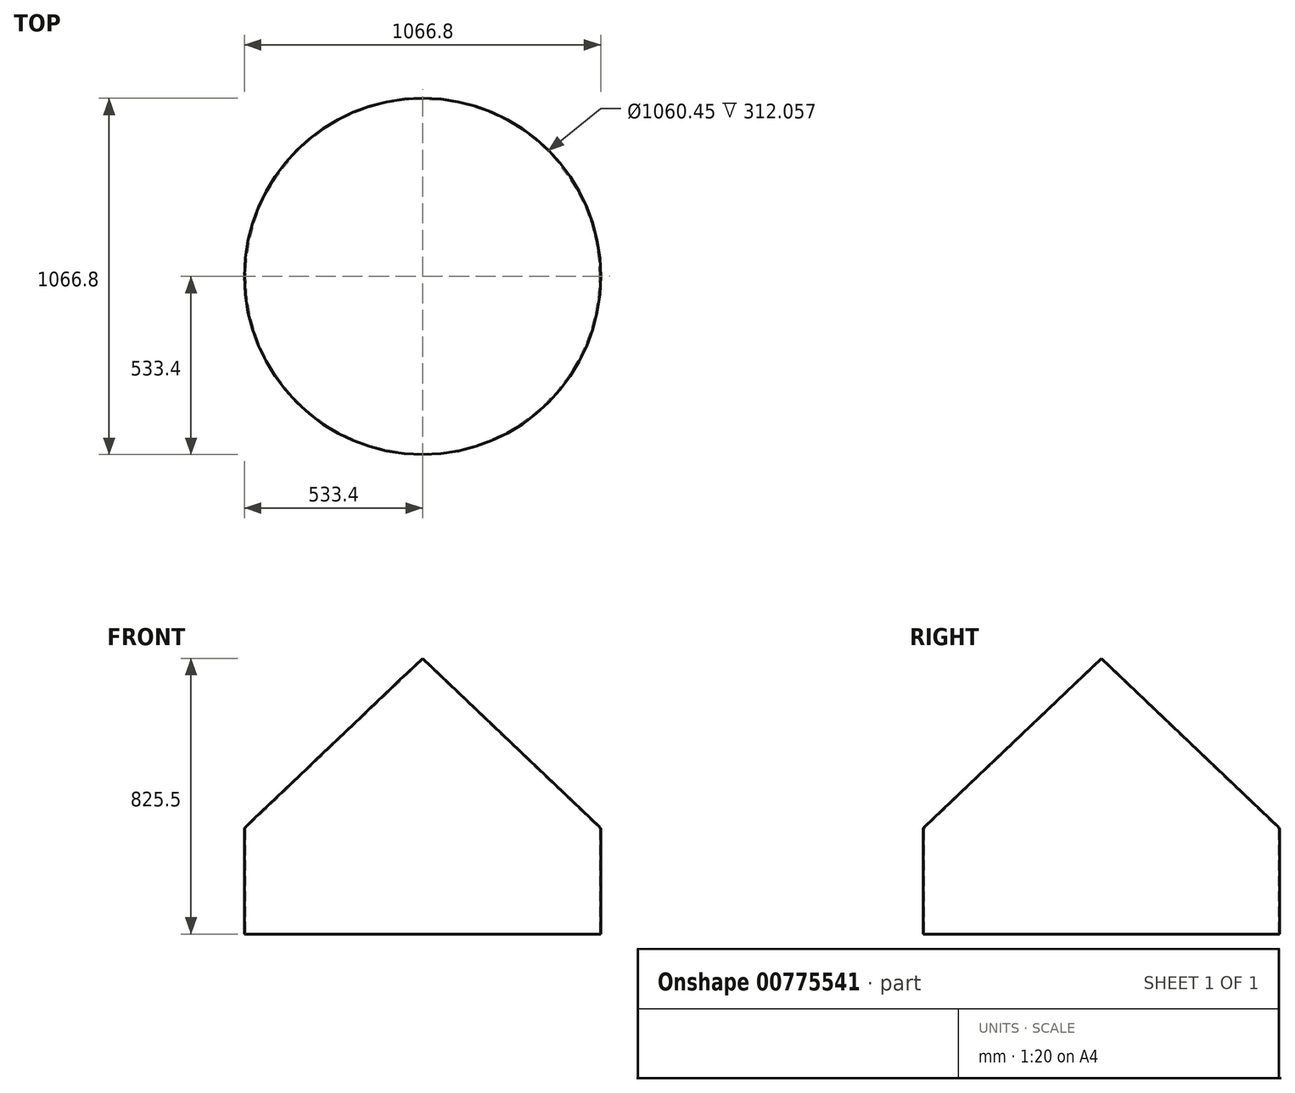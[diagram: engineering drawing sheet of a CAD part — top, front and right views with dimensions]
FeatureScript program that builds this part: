
annotation { "Feature Type Name" : "Feature", "Feature Type Description" : "" }
export const myFeature = defineFeature(function(context is Context, id is Id, definition is map)
    precondition{}
    {
        {
            var Q0;
            Q0=qCreatedBy(makeId("Front.planeOp"),FACE);
            var sketch = newSketch(context, id + "F0", { "sketchPlane" : qUnion([Q0])});
            skLineSegment(sketch, "E0.bottom", {"start": v(0, 0) * mm, "end": v(533.4, 0) * mm});
            skLineSegment(sketch, "E0.left", {"start": v(0, 0) * mm, "end": v(0, 825.5) * mm});
            skLineSegment(sketch, "E0.right", {"start": v(533.4, 0) * mm, "end": v(533.4, 317.5) * mm});
            skLineSegment(sketch, "E1", {"start": v(533.4, 317.5) * mm, "end": v(0, 825.5) * mm});
            skSolve(sketch);
        }
        {
            var Q0;
            Q0 = qSketchRegion(id + "F0", true);
            var Q1;
            Q1=sQuery(id+"F0.wireOp",EDGE,"E0.left");
            revolve(context, id + "F1", {"surfaceOperationType" : NewSurfaceOperationType.NEW, "entities" : qUnion([Q0]), "axis" : qUnion([Q1]), "revolveType" : RevolveType.FULL});
        }
        {
            var Q0;
            Q0=makeQuery(id+"F1.opRevolve","SWEPT_EDGE",EDGE,{"disambiguationData":[OSD([sQuery(id+"F0.wireOp",EDGE,"E0.right"),sQuery(id+"F0.wireOp",EDGE,"E1")])]});
            fillet(context, id + "F2", {"entities" : qUnion([Q0]), "radius" : 12.7 * mm, "tangentPropagation" : true, "allowEdgeOverflow" : false});
        }
        {
            var Q0;
            Q0=makeQuery(id+"F1.opRevolve","SWEPT_FACE",FACE,{"disambiguationData":[OSD([sQuery(id+"F0.wireOp",EDGE,"E0.bottom")])]});
            shell(context, id + "F3", {"entities" : qUnion([Q0]), "thickness" : 3.17 * mm});
        }
    });
